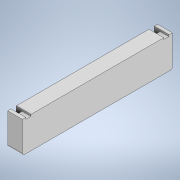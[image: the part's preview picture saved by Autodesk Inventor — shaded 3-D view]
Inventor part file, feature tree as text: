
AUTODESK INVENTOR PART (.ipt)
format: ipt  version: 2022 (Build 260153000, 153)  size: 205,824 bytes
history: native  units: mm
features: sketch x4, extrude x4, fillet x1, projected_geometry x1
ambient origin geometry x8: Origin, YZ Plane, XZ Plane, XY Plane, X Axis, Y Axis, Z Axis, Center Point
bodies: Solid1 (feature_tree)
feature tree (10):
  sketch  "Sketch1"  dims[d0=87.28mm d1=3.0mm]
  extrude  "Extrusion1"  Depth=3.0mm
  extrude  "Extrusion2"  Depth=2.0mm
  extrude  "Extrusion4"  Depth=3.0mm
  extrude  "Extrusion5"  Depth=1.25mm
  fillet  "Fillet1"  Radius=0.1mm
  sketch  "Sketch2"  dims[d2=0.125mm d3=2.0mm]
  sketch  "Sketch3"  dims[d4=12.0mm d5=3.0mm]
  projected_geometry  "Projected Loop1"
  sketch  "Sketch4"  dims[d6=12.0mm d7=3.0mm d8=0.1mm d9=0.1mm d10=0.0mm d11=0.0mm d12=6.5mm d13=0.0mm d14=0.2mm d15=1.0mm d16=0.0mm d17=0.0mm d18=0.2mm d19=1.0mm d20=0.0mm d21=0.0mm d22=29.75mm d23=0.0mm d24=0.0mm d25=28.89mm d26=2.85mm d27=0.0mm d30=2.5mm d31=0.0mm d32=2.5mm d33=0.0mm d34=1.25mm]
